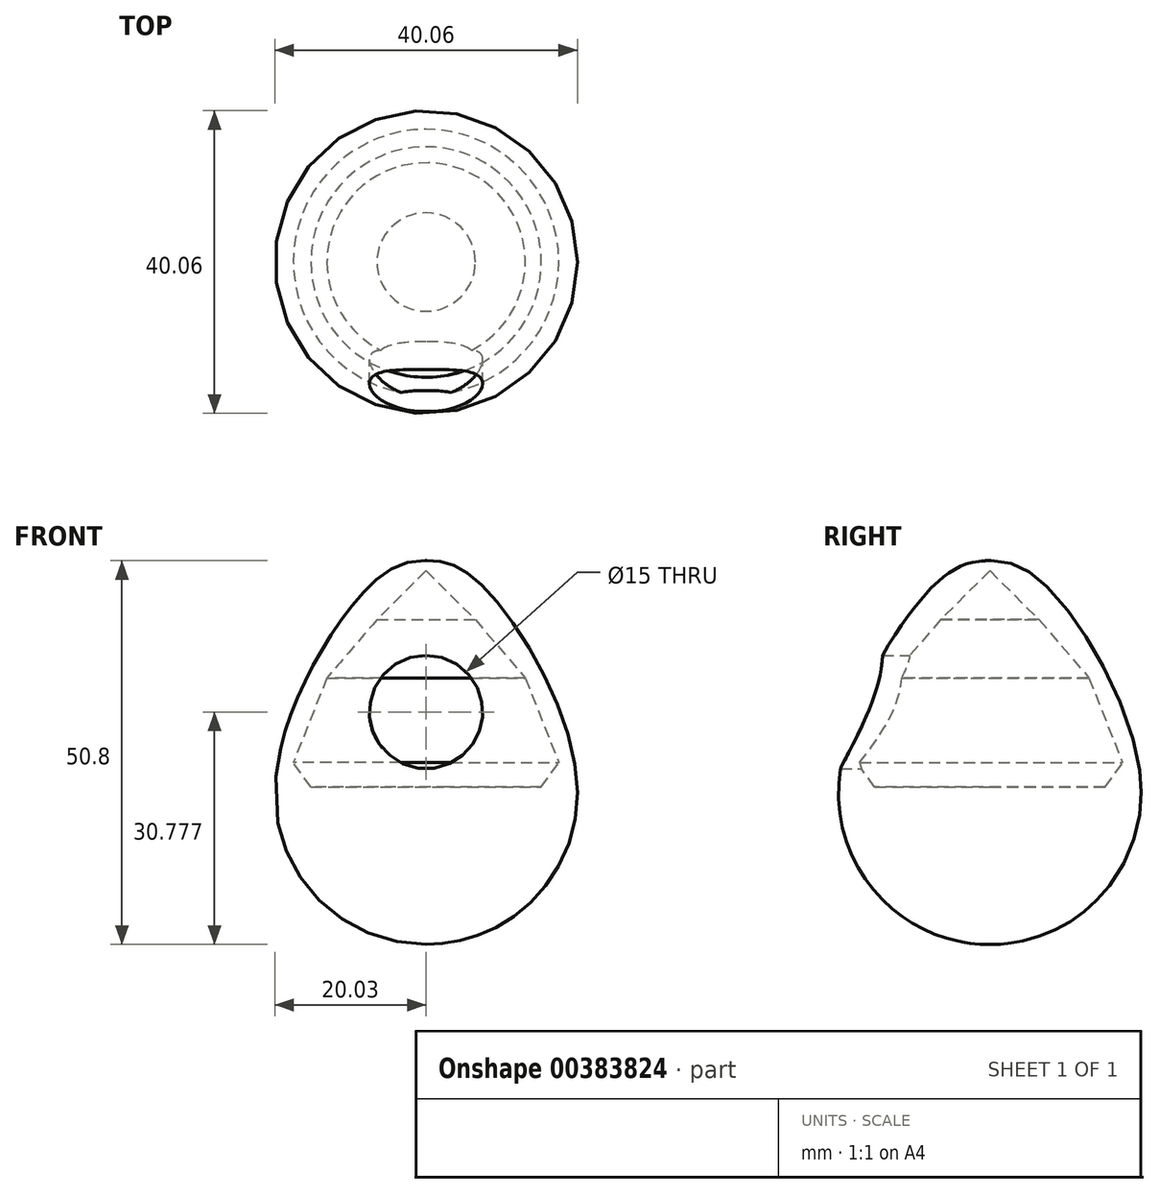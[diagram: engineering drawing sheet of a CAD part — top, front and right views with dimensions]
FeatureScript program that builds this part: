
annotation { "Feature Type Name" : "Feature", "Feature Type Description" : "" }
export const myFeature = defineFeature(function(context is Context, id is Id, definition is map)
    precondition{}
    {
        {
            var Q0;
            Q0=qCreatedBy(makeId("Front.planeOp"),FACE);
            var sketch = newSketch(context, id + "F0", { "sketchPlane" : qUnion([Q0])});
            skLineSegment(sketch, "E0", {"start": v(0, 0) * mm, "end": v(0, 69.22) * mm, "construction": true});
            skFitSpline(sketch, "E1", {"points": [v(0, 0) * mm, v(11.45, 3.6) * mm, v(20.02, 20.84) * mm, v(7.5, 47.43) * mm, v(0, 50.8) * mm], "startDerivative": vector(47.95, 0) * mm, "endDerivative": vector(-44.76, -0.47) * mm});
            skLineSegment(sketch, "E2", {"start": v(0, 0) * mm, "end": v(0, 20.84) * mm});
            skLineSegment(sketch, "E3", {"start": v(0, 20.84) * mm, "end": v(15.25, 20.84) * mm});
            skLineSegment(sketch, "E4", {"start": v(6.51, 42.98) * mm, "end": v(0, 49.5) * mm});
            skLineSegment(sketch, "E5", {"start": v(0, 49.5) * mm, "end": v(0, 50.8) * mm});
            skLineSegment(sketch, "E6", {"start": v(6.51, 42.98) * mm, "end": v(13.13, 35.29) * mm});
            skLineSegment(sketch, "E7", {"start": v(13.13, 35.29) * mm, "end": v(17.57, 24.06) * mm});
            skLineSegment(sketch, "E8", {"start": v(17.57, 24.06) * mm, "end": v(15.25, 20.84) * mm});
            skSolve(sketch);
        }
        {
            var Q0;
            Q0=makeQuery(id+"F0.imprint","IMPRINT",FACE,{"disambiguationData":[TD([[makeQuery(id+"F0.imprint","IMPRINT",EDGE,{"derivedFrom":sQuery(id+"F0.wireOp",EDGE,"E1")}),1.0]])]});
            var Q1;
            Q1=sQuery(id+"F0.wireOp",EDGE,"E0");
            revolve(context, id + "F1", {"entities" : qUnion([Q0]), "axis" : qUnion([Q1]), "revolveType" : RevolveType.FULL});
        }
        {
            var Q0;
            Q0=qCreatedBy(makeId("Front.planeOp"),FACE);
            var sketch = newSketch(context, id + "F2", { "sketchPlane" : qUnion([Q0])});
            skCircle(sketch, "E9", {"center": v(0, 30.78) * mm, "radius": 7.5 * mm});
            skSolve(sketch);
        }
        {
            var Q0;
            Q0 = qSketchRegion(id + "F2", true);
            extrude(context, id + "F3", {"entities" : qUnion([Q0]), "operationType" : NewBodyOperationType.REMOVE, "depth" : 22.5 * mm});
        }
    });
